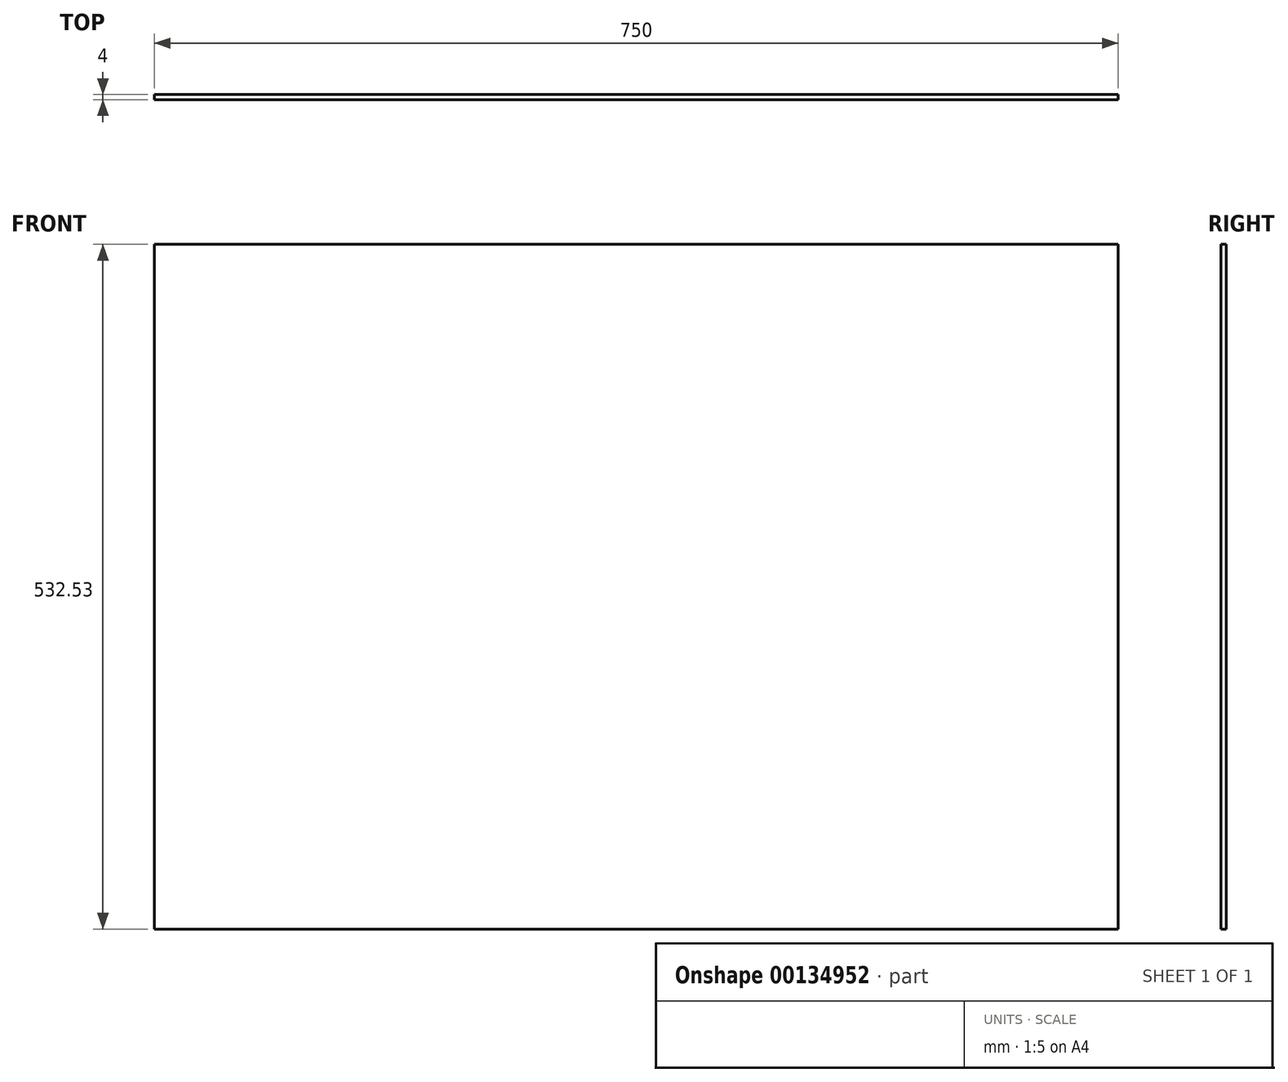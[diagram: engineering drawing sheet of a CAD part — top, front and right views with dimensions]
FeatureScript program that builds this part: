
annotation { "Feature Type Name" : "Feature", "Feature Type Description" : "" }
export const myFeature = defineFeature(function(context is Context, id is Id, definition is map)
    precondition{}
    {
        {
            var Q0;
            Q0=qCreatedBy(makeId("Front.planeOp"),FACE);
            var sketch = newSketch(context, id + "F0", { "sketchPlane" : qUnion([Q0])});
            skLineSegment(sketch, "E0.bottom", {"start": v(0, 0) * mm, "end": v(750, 0) * mm});
            skLineSegment(sketch, "E0.top", {"start": v(0, 532.53) * mm, "end": v(750, 532.53) * mm});
            skLineSegment(sketch, "E0.left", {"start": v(0, 0) * mm, "end": v(0, 532.53) * mm});
            skLineSegment(sketch, "E0.right", {"start": v(750, 0) * mm, "end": v(750, 532.53) * mm});
            skSolve(sketch);
        }
        {
            var Q0;
            Q0=makeQuery(id+"F0.imprint","IMPRINT",FACE,{"disambiguationData":[TD([[makeQuery(id+"F0.imprint","IMPRINT",EDGE,{"derivedFrom":sQuery(id+"F0.wireOp",EDGE,"E0.bottom")}),1.0]])]});
            extrude(context, id + "F1", {"entities" : qUnion([Q0]), "depth" : 4 * mm});
        }
    });
